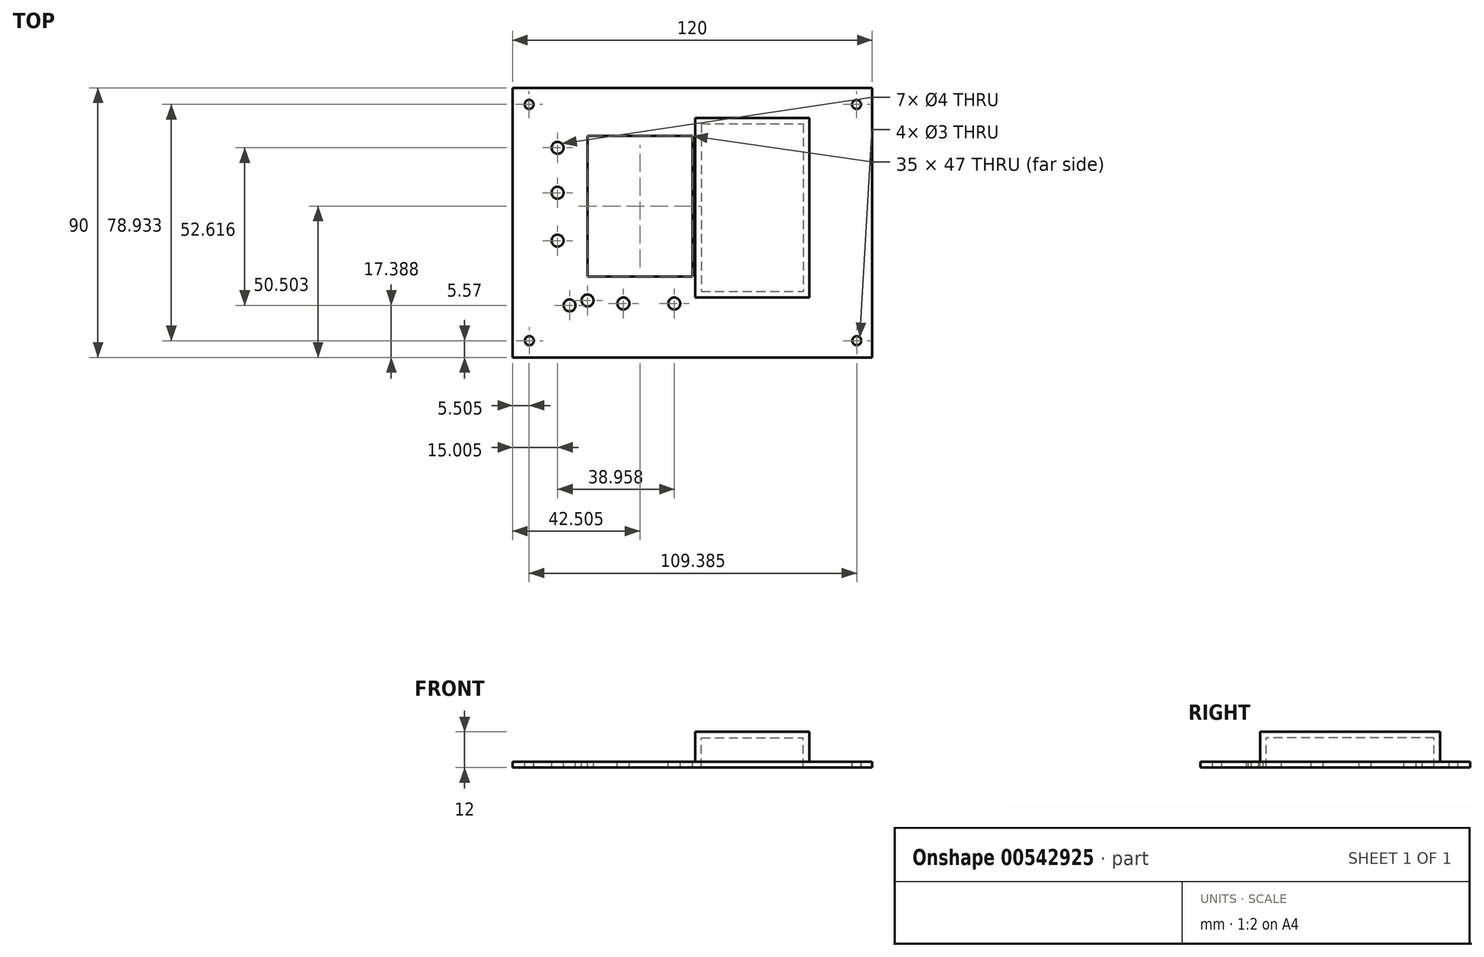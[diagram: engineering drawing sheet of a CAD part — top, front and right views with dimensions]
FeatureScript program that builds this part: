
annotation { "Feature Type Name" : "Feature", "Feature Type Description" : "" }
export const myFeature = defineFeature(function(context is Context, id is Id, definition is map)
    precondition{}
    {
        {
            var Q0;
            Q0=qCreatedBy(makeId("Top.planeOp"),FACE);
            var sketch = newSketch(context, id + "F0", { "sketchPlane" : qUnion([Q0])});
            skLineSegment(sketch, "E0.bottom", {"start": v(-80.19, 55.43) * mm, "end": v(39.81, 55.43) * mm});
            skLineSegment(sketch, "E0.top", {"start": v(-80.19, -34.57) * mm, "end": v(39.81, -34.57) * mm});
            skLineSegment(sketch, "E0.left", {"start": v(-80.19, 55.43) * mm, "end": v(-80.19, -34.57) * mm});
            skLineSegment(sketch, "E0.right", {"start": v(39.81, 55.43) * mm, "end": v(39.81, -34.57) * mm});
            skSolve(sketch);
        }
        {
            var Q0;
            Q0=makeQuery(id+"F0.imprint","IMPRINT",FACE,{"disambiguationData":[TD([[makeQuery(id+"F0.imprint","IMPRINT",EDGE,{"derivedFrom":sQuery(id+"F0.wireOp",EDGE,"E0.bottom")}),-1.0]])]});
            extrude(context, id + "F1", {"entities" : qUnion([Q0]), "depth" : 2 * mm, "offsetDistance" : 25 * mm});
        }
        {
            var Q0;
            Q0=makeQuery(id+"F1.opExtrude","CAP_FACE",FACE,{"disambiguationData":[OSD([sQuery(id+"F0.wireOp",EDGE,"E0.bottom"),sQuery(id+"F0.wireOp",EDGE,"E0.top"),sQuery(id+"F0.wireOp",EDGE,"E0.left"),sQuery(id+"F0.wireOp",EDGE,"E0.right")])],"isStart":false});
            var sketch = newSketch(context, id + "F2", { "sketchPlane" : qUnion([Q0])});
            skLineSegment(sketch, "E1.bottom", {"start": v(-55.19, 39.43) * mm, "end": v(-20.19, 39.43) * mm});
            skLineSegment(sketch, "E1.top", {"start": v(-55.19, -7.57) * mm, "end": v(-20.19, -7.57) * mm});
            skLineSegment(sketch, "E1.left", {"start": v(-55.19, 39.43) * mm, "end": v(-55.19, -7.57) * mm});
            skLineSegment(sketch, "E1.right", {"start": v(-20.19, 39.43) * mm, "end": v(-20.19, -7.57) * mm});
            skLineSegment(sketch, "E2.bottom", {"start": v(-19.19, 45.43) * mm, "end": v(18.81, 45.43) * mm});
            skLineSegment(sketch, "E2.top", {"start": v(-19.19, -14.57) * mm, "end": v(18.81, -14.57) * mm});
            skLineSegment(sketch, "E2.left", {"start": v(-19.19, 45.43) * mm, "end": v(-19.19, -14.57) * mm});
            skLineSegment(sketch, "E2.right", {"start": v(18.81, 45.43) * mm, "end": v(18.81, -14.57) * mm});
            skLineSegment(sketch, "E3.bottom", {"start": v(-18.17, 43.7) * mm, "end": v(17.8, 43.7) * mm});
            skLineSegment(sketch, "E3.top", {"start": v(-18.17, -12.84) * mm, "end": v(17.8, -12.84) * mm});
            skLineSegment(sketch, "E3.left", {"start": v(-18.17, 43.7) * mm, "end": v(-18.17, -12.84) * mm});
            skLineSegment(sketch, "E3.right", {"start": v(17.8, 43.7) * mm, "end": v(17.8, -12.84) * mm});
            skPoint(sketch, "E3.middle", {"position": v(-0.19, 15.43) * mm});
            skPoint(sketch, "E3.middle.positionSnap0", {"position": v(-19.19, 15.43) * mm});
            skPoint(sketch, "E3.middle.positionSnap1", {"position": v(-0.19, 45.43) * mm});
            skPoint(sketch, "E3.centerSnap0", {"position": v(-19.19, 15.43) * mm});
            skPoint(sketch, "E3.centerSnap1", {"position": v(-0.19, 45.43) * mm});
            skSolve(sketch);
        }
        {
            var Q0;
            Q0=makeQuery(id+"F2.imprint","IMPRINT",FACE,{"disambiguationData":[TD([[makeQuery(id+"F2.imprint","IMPRINT",EDGE,{"derivedFrom":sQuery(id+"F2.wireOp",EDGE,"E1.bottom")}),-1.0]])]});
            extrude(context, id + "F3", {"entities" : qUnion([Q0]), "operationType" : NewBodyOperationType.REMOVE, "oppositeDirection" : true, "depth" : 2 * mm, "offsetDistance" : 25 * mm});
        }
        {
            var Q0;
            Q0=makeQuery(id+"F1.opExtrude","CAP_FACE",FACE,{"disambiguationData":[OSD([sQuery(id+"F0.wireOp",EDGE,"E0.bottom"),sQuery(id+"F0.wireOp",EDGE,"E0.top"),sQuery(id+"F0.wireOp",EDGE,"E0.left"),sQuery(id+"F0.wireOp",EDGE,"E0.right")])],"isStart":false});
            var sketch = newSketch(context, id + "F4", { "sketchPlane" : qUnion([Q0])});
            skLineSegment(sketch, "E4.bottom", {"start": v(-77.19, 52.43) * mm, "end": v(36.81, 52.43) * mm});
            skLineSegment(sketch, "E4.top", {"start": v(-77.19, -31.57) * mm, "end": v(36.81, -31.57) * mm});
            skLineSegment(sketch, "E4.left", {"start": v(-77.19, 52.43) * mm, "end": v(-77.19, -31.57) * mm});
            skLineSegment(sketch, "E4.right", {"start": v(36.81, 52.43) * mm, "end": v(36.81, -31.57) * mm});
            skPoint(sketch, "E4.middle", {"position": v(-20.19, 10.43) * mm});
            skPoint(sketch, "E4.middle.positionSnap0", {"position": v(-20.19, 55.43) * mm});
            skPoint(sketch, "E4.middle.positionSnap1", {"position": v(-80.19, 10.43) * mm});
            skPoint(sketch, "E4.centerSnap0", {"position": v(-20.19, 55.43) * mm});
            skPoint(sketch, "E4.centerSnap1", {"position": v(-80.19, 10.43) * mm});
            skLineSegment(sketch, "E5.bottom", {"start": v(-77.19, 52.43) * mm, "end": v(-72.19, 52.43) * mm});
            skLineSegment(sketch, "E5.top", {"start": v(-77.19, 47.43) * mm, "end": v(-72.19, 47.43) * mm});
            skLineSegment(sketch, "E5.left", {"start": v(-77.19, 52.43) * mm, "end": v(-77.19, 47.43) * mm});
            skLineSegment(sketch, "E5.right", {"start": v(-72.19, 52.43) * mm, "end": v(-72.19, 47.43) * mm});
            skLineSegment(sketch, "E6.0.1.0", {"start": v(-72.1, -26.6) * mm, "end": v(-72.1, -31.6) * mm});
            skLineSegment(sketch, "E6.0.1.1", {"start": v(-77.1, -31.6) * mm, "end": v(-72.1, -31.6) * mm});
            skLineSegment(sketch, "E6.0.1.2", {"start": v(-77.1, -26.6) * mm, "end": v(-77.1, -31.6) * mm});
            skLineSegment(sketch, "E6.0.1.3", {"start": v(-77.1, -26.6) * mm, "end": v(-72.1, -26.6) * mm});
            skLineSegment(sketch, "E6.1.0.0", {"start": v(36.9, 52.4) * mm, "end": v(36.9, 47.4) * mm});
            skLineSegment(sketch, "E6.1.0.1", {"start": v(31.9, 47.4) * mm, "end": v(36.9, 47.4) * mm});
            skLineSegment(sketch, "E6.1.0.2", {"start": v(31.9, 52.4) * mm, "end": v(31.9, 47.4) * mm});
            skLineSegment(sketch, "E6.1.0.3", {"start": v(31.9, 52.4) * mm, "end": v(36.9, 52.4) * mm});
            skLineSegment(sketch, "E6.1.1.0", {"start": v(36.99, -26.63) * mm, "end": v(36.99, -31.63) * mm});
            skLineSegment(sketch, "E6.1.1.1", {"start": v(31.99, -31.63) * mm, "end": v(36.99, -31.63) * mm});
            skLineSegment(sketch, "E6.1.1.2", {"start": v(31.99, -26.63) * mm, "end": v(31.99, -31.63) * mm});
            skLineSegment(sketch, "E6.1.1.3", {"start": v(31.99, -26.63) * mm, "end": v(36.99, -26.63) * mm});
            skLineSegment(sketch, "E6.direction1", {"start": v(-72.19, 47.43) * mm, "end": v(36.9, 47.4) * mm, "construction": true});
            skLineSegment(sketch, "E6.direction2", {"start": v(-72.19, 47.43) * mm, "end": v(-72.1, -31.6) * mm, "construction": true});
            skCircle(sketch, "E7", {"center": v(-74.69, 49.93) * mm, "radius": 1.5 * mm});
            skPoint(sketch, "E7.centerSnap0", {"position": v(-74.69, 52.43) * mm});
            skPoint(sketch, "E7.centerSnap1", {"position": v(-77.19, 49.93) * mm});
            skCircle(sketch, "E8.0.1.0", {"center": v(-74.6, -29) * mm, "radius": 1.5 * mm});
            skCircle(sketch, "E8.1.0.0", {"center": v(34.61, 49.93) * mm, "radius": 1.5 * mm});
            skCircle(sketch, "E8.1.1.0", {"center": v(34.7, -29) * mm, "radius": 1.5 * mm});
            skLineSegment(sketch, "E8.direction1", {"start": v(-74.69, 49.93) * mm, "end": v(34.61, 49.93) * mm, "construction": true});
            skLineSegment(sketch, "E8.direction2", {"start": v(-74.69, 49.93) * mm, "end": v(-74.6, -29) * mm, "construction": true});
            skSolve(sketch);
        }
        {
            var Q0;
            Q0=sQuery(id+"F4.wireOp",VERTEX,"E8.direction2.end");
            var Q1;
            Q1=sQuery(id+"F4.wireOp",VERTEX,"E8.1.1.0.center");
            var Q2;
            Q2=sQuery(id+"F4.wireOp",VERTEX,"E8.direction1.end");
            var Q3;
            Q3=sQuery(id+"F4.wireOp",VERTEX,"E8.direction1.start");
            var Q4;
            Q4=makeQuery(id+"F1.opExtrude","SWEPT_BODY",BODY,{"disambiguationData":[OSD([sQuery(id+"F0.wireOp",EDGE,"E0.bottom"),sQuery(id+"F0.wireOp",EDGE,"E0.top"),sQuery(id+"F0.wireOp",EDGE,"E0.left"),sQuery(id+"F0.wireOp",EDGE,"E0.right")])]});
            hole(context, id + "F5", {"style" : HoleStyle.SIMPLE, "endStyle" : HoleEndStyle.THROUGH, "holeDiameter" : 3 * mm, "isTappedThrough" : true, "tappedDepth" : 12 * mm, "tapClearance" : 3, "locations" : qUnion([Q0, Q1, Q2, Q3]), "scope" : qUnion([Q4])});
        }
        {
            var Q0;
            Q0=makeQuery(id+"F1.opExtrude","CAP_FACE",FACE,{"disambiguationData":[OSD([sQuery(id+"F0.wireOp",EDGE,"E0.bottom"),sQuery(id+"F0.wireOp",EDGE,"E0.top"),sQuery(id+"F0.wireOp",EDGE,"E0.left"),sQuery(id+"F0.wireOp",EDGE,"E0.right")])],"isStart":false});
            var sketch = newSketch(context, id + "F6", { "sketchPlane" : qUnion([Q0])});
            skLineSegment(sketch, "E9.bottom", {"start": v(-19.19, 45.43) * mm, "end": v(18.81, 45.43) * mm});
            skLineSegment(sketch, "E9.top", {"start": v(-19.19, -14.57) * mm, "end": v(18.81, -14.57) * mm});
            skLineSegment(sketch, "E9.left", {"start": v(-19.19, 45.43) * mm, "end": v(-19.19, -14.57) * mm});
            skLineSegment(sketch, "E9.right", {"start": v(18.81, 45.43) * mm, "end": v(18.81, -14.57) * mm});
            skLineSegment(sketch, "E10.bottom", {"start": v(-17.19, 43.43) * mm, "end": v(16.81, 43.43) * mm});
            skLineSegment(sketch, "E10.top", {"start": v(-17.19, -12.57) * mm, "end": v(16.81, -12.57) * mm});
            skLineSegment(sketch, "E10.left", {"start": v(-17.19, 43.43) * mm, "end": v(-17.19, -12.57) * mm});
            skLineSegment(sketch, "E10.right", {"start": v(16.81, 43.43) * mm, "end": v(16.81, -12.57) * mm});
            skPoint(sketch, "E10.middle", {"position": v(-0.19, 15.43) * mm});
            skPoint(sketch, "E10.middle.positionSnap0", {"position": v(-19.19, 15.43) * mm});
            skPoint(sketch, "E10.middle.positionSnap1", {"position": v(-0.19, 45.43) * mm});
            skPoint(sketch, "E10.centerSnap0", {"position": v(-19.19, 15.43) * mm});
            skPoint(sketch, "E10.centerSnap1", {"position": v(-0.19, 45.43) * mm});
            skSolve(sketch);
        }
        {
            var Q0;
            Q0 = qSketchRegion(id + "F6", true);
            var Q1;
            Q1=makeQuery(id+"F6.imprint","IMPRINT",FACE,{"disambiguationData":[TD([[makeQuery(id+"F6.imprint","IMPRINT",EDGE,{"derivedFrom":sQuery(id+"F6.wireOp",EDGE,"E10.bottom")}),-1.0]])]});
            extrude(context, id + "F7", {"entities" : qUnion([Q0, Q1]), "operationType" : NewBodyOperationType.ADD, "depth" : 10 * mm, "offsetDistance" : 25 * mm});
        }
        {
            var Q0;
            Q0=makeQuery(id+"F7.opExtrude","CAP_FACE",FACE,{"disambiguationData":[OSD([sQuery(id+"F6.wireOp",EDGE,"E9.bottom"),sQuery(id+"F6.wireOp",EDGE,"E9.top"),sQuery(id+"F6.wireOp",EDGE,"E9.left"),sQuery(id+"F6.wireOp",EDGE,"E9.right")])],"isStart":false});
            var sketch = newSketch(context, id + "F8", { "sketchPlane" : qUnion([Q0])});
            skLineSegment(sketch, "E11.bottom", {"start": v(-17.19, 43.43) * mm, "end": v(16.81, 43.43) * mm});
            skLineSegment(sketch, "E11.top", {"start": v(-17.19, -12.57) * mm, "end": v(16.81, -12.57) * mm});
            skLineSegment(sketch, "E11.left", {"start": v(-17.19, 43.43) * mm, "end": v(-17.19, -12.57) * mm});
            skLineSegment(sketch, "E11.right", {"start": v(16.81, 43.43) * mm, "end": v(16.81, -12.57) * mm});
            skPoint(sketch, "E11.middle", {"position": v(-0.19, 15.43) * mm});
            skPoint(sketch, "E11.middle.positionSnap0", {"position": v(-19.19, 15.43) * mm});
            skPoint(sketch, "E11.middle.positionSnap1", {"position": v(-0.19, 45.43) * mm});
            skPoint(sketch, "E11.centerSnap0", {"position": v(-19.19, 15.43) * mm});
            skPoint(sketch, "E11.centerSnap1", {"position": v(-0.19, 45.43) * mm});
            skSolve(sketch);
        }
        {
            var Q0;
            Q0 = qSketchRegion(id + "F8", true);
            extrude(context, id + "F9", {"entities" : qUnion([Q0]), "operationType" : NewBodyOperationType.REMOVE, "endBound" : BoundingType.THROUGH_ALL, "oppositeDirection" : true, "depth" : 25 * mm, "offsetDistance" : 25 * mm});
        }
        {
            var Q0;
            Q0=makeQuery(id+"F7.opExtrude","CAP_FACE",FACE,{"disambiguationData":[OSD([sQuery(id+"F6.wireOp",EDGE,"E9.bottom"),sQuery(id+"F6.wireOp",EDGE,"E9.top"),sQuery(id+"F6.wireOp",EDGE,"E9.left"),sQuery(id+"F6.wireOp",EDGE,"E9.right")])],"isStart":false});
            var sketch = newSketch(context, id + "F10", { "sketchPlane" : qUnion([Q0])});
            skLineSegment(sketch, "E12.bottom", {"start": v(-17.19, 43.43) * mm, "end": v(16.81, 43.43) * mm});
            skLineSegment(sketch, "E12.top", {"start": v(-17.19, -12.57) * mm, "end": v(16.81, -12.57) * mm});
            skLineSegment(sketch, "E12.left", {"start": v(-17.19, 43.43) * mm, "end": v(-17.19, -12.57) * mm});
            skLineSegment(sketch, "E12.right", {"start": v(16.81, 43.43) * mm, "end": v(16.81, -12.57) * mm});
            skSolve(sketch);
        }
        {
            var Q0;
            Q0=makeQuery(id+"F10.imprint","IMPRINT",FACE,{"disambiguationData":[TD([[makeQuery(id+"F10.imprint","IMPRINT",EDGE,{"derivedFrom":sQuery(id+"F10.wireOp",EDGE,"E12.bottom")}),-1.0]])]});
            extrude(context, id + "F11", {"entities" : qUnion([Q0]), "operationType" : NewBodyOperationType.ADD, "oppositeDirection" : true, "depth" : 2 * mm, "offsetDistance" : 25 * mm});
        }
        {
            var Q0;
            Q0=makeQuery(id+"F1.opExtrude","CAP_FACE",FACE,{"disambiguationData":[OSD([sQuery(id+"F0.wireOp",EDGE,"E0.bottom"),sQuery(id+"F0.wireOp",EDGE,"E0.top"),sQuery(id+"F0.wireOp",EDGE,"E0.left"),sQuery(id+"F0.wireOp",EDGE,"E0.right")])],"isStart":false});
            var sketch = newSketch(context, id + "F12", { "sketchPlane" : qUnion([Q0])});
            skCircle(sketch, "E13", {"center": v(-65.19, 35.43) * mm, "radius": 2 * mm});
            skCircle(sketch, "E14", {"center": v(-65.19, 20.43) * mm, "radius": 2 * mm});
            skCircle(sketch, "E15", {"center": v(-65.19, 4.43) * mm, "radius": 2 * mm});
            skCircle(sketch, "E16", {"center": v(-61.19, -17.18) * mm, "radius": 2 * mm});
            skCircle(sketch, "E17", {"center": v(-55.19, -15.57) * mm, "radius": 2 * mm});
            skCircle(sketch, "E18", {"center": v(-43.23, -16.57) * mm, "radius": 2 * mm});
            skCircle(sketch, "E19", {"center": v(-26.23, -16.57) * mm, "radius": 2 * mm});
            skSolve(sketch);
        }
        {
            var Q0;
            Q0 = qSketchRegion(id + "F12", true);
            extrude(context, id + "F13", {"entities" : qUnion([Q0]), "operationType" : NewBodyOperationType.REMOVE, "oppositeDirection" : true, "depth" : 25 * mm, "offsetDistance" : 25 * mm});
        }
    });
